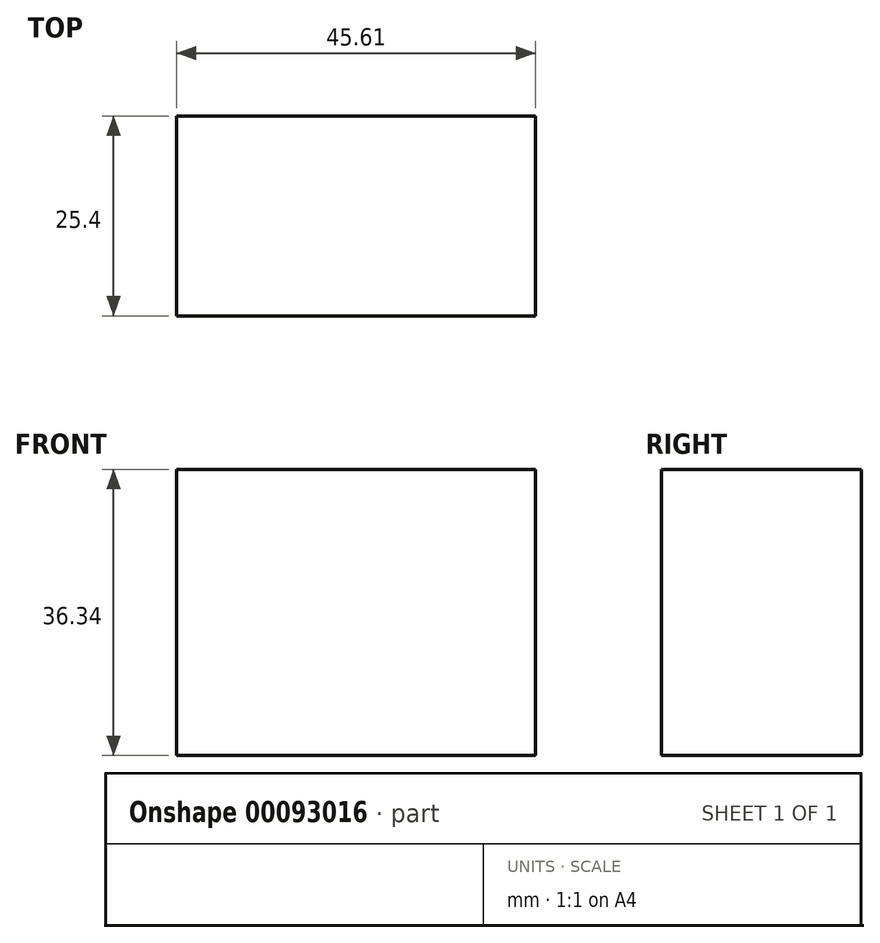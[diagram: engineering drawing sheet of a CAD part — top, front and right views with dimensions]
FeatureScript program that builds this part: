
annotation { "Feature Type Name" : "Feature", "Feature Type Description" : "" }
export const myFeature = defineFeature(function(context is Context, id is Id, definition is map)
    precondition{}
    {
        {
            var Q0;
            Q0=qCreatedBy(makeId("Front.planeOp"),FACE);
            var sketch = newSketch(context, id + "F0", { "sketchPlane" : qUnion([Q0])});
            skLineSegment(sketch, "E0", {"start": v(0, 0) * mm, "end": v(0, 36.34) * mm});
            skLineSegment(sketch, "E1", {"start": v(0, 36.34) * mm, "end": v(45.6, 36.34) * mm});
            skLineSegment(sketch, "E2", {"start": v(45.6, 36.34) * mm, "end": v(45.6, 0) * mm});
            skLineSegment(sketch, "E3", {"start": v(45.6, 0) * mm, "end": v(0, 0) * mm});
            skSolve(sketch);
        }
        {
            var Q0;
            Q0=makeQuery(id+"F0.imprint","IMPRINT",FACE,{"disambiguationData":[TD([[makeQuery(id+"F0.imprint","IMPRINT",EDGE,{"derivedFrom":sQuery(id+"F0.wireOp",EDGE,"E0")}),-1.0]])]});
            extrude(context, id + "F1", {"entities" : qUnion([Q0]), "depth" : 25.4 * mm});
        }
    });
